# Revit family: Deca_Desviador para chuveiro luxo_1982.C.LUX.330
name_source: partatom
category: Plumbing Fixtures
revit_build: Autodesk Revit Architecture 2012 (Build: 20120126_0600(x64)
units: mm (PartAtom-declared; Revit-internal decimal feet)

## types (1)
- 1982.C.LUX.330_Cromado CR10
    Acompanha o Produto = Flexível de 1,80m
    Aprovado por = Contino/quattroD
    Assembly Code = D2010
    Atendimento ao Cliente = 0800-0117075
    CWFU = 0
    Criado por = Contino/quattroD
    Código = 1982.C.LUX.330
    Default Elevation = 2000 mm  [stored 6.56168 ft]
    Description = Desviador para chuveiro
    Desviador = Deca Cromado Metal CR10
    Diâmetro Água Fria = 15 mm  [stored 0.0492126 ft]
    Flor Pressure = 0.00 psi
    Informações Complementares = Recomendável com pressão mínima de 8 m.c.a para aquecedor de passagem e de 4 m.c.a. para aquecedor de acumulação.
    Linha = Desviadores
    Louça/Metais = Metal
    Manufacturer = Deca
    Material = Latão Cromado e Plástico de Engenharia
    Model = 1982.C.LUX.330
    Norma = ABNT NBR 10283:2003
    Peso Liquido (Kg) = 1.64
    Pressão = 2 A 40 mca
    Produto = Desviador para chuveiro luxo
    Raio Água Fria = 8 mm  [stored 0.0262467 ft]
    Segmento = Luxo
    URL = www.deca.com.br/produtos
    Variações de COR = Cromado (1982.C.LUX.330)

note: [stored X ft] marks values corroborated as IEEE doubles in the binary element streams (Revit-internal decimal feet)

## geometry (parser evidence)
native form markers: Blend x4, Sweep x2
no freeform markers — native parametric forms only
